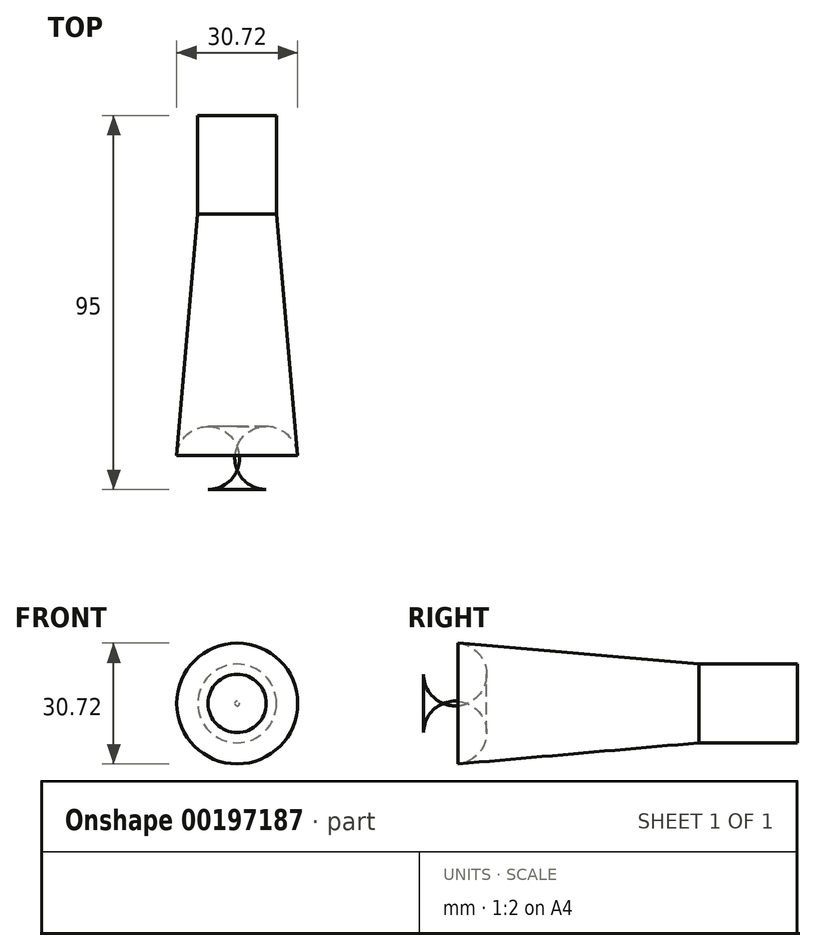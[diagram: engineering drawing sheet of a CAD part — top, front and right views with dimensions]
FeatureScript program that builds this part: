
annotation { "Feature Type Name" : "Feature", "Feature Type Description" : "" }
export const myFeature = defineFeature(function(context is Context, id is Id, definition is map)
    precondition{}
    {
        {
            var Q0;
            Q0=qCreatedBy(makeId("Front.planeOp"),FACE);
            var sketch = newSketch(context, id + "F0", { "sketchPlane" : qUnion([Q0])});
            skCircle(sketch, "E0", {"center": v(0, 0) * mm, "radius": 10 * mm});
            skSolve(sketch);
        }
        {
            var Q0;
            Q0 = qSketchRegion(id + "F0", true);
            extrude(context, id + "F1", {"entities" : qUnion([Q0]), "depth" : 70 * mm, "hasDraft" : true, "draftAngle" : 5 * degree});
        }
        {
            var Q0;
            Q0=makeQuery(id+"F1.opExtrude","CAP_EDGE",EDGE,{"disambiguationData":[OSD([sQuery(id+"F0.wireOp",EDGE,"E0")])],"isStart":false});
            fillet(context, id + "F2", {"entities" : qUnion([Q0]), "radius" : 8 * mm, "tangentPropagation" : true, "allowEdgeOverflow" : false});
        }
        {
            var Q0;
            Q0=makeQuery(id+"F1.opExtrude","CAP_FACE",FACE,{"disambiguationData":[OSD([sQuery(id+"F0.wireOp",EDGE,"E0")])],"isStart":true});
            var sketch = newSketch(context, id + "F3", { "sketchPlane" : qUnion([Q0])});
            skCircle(sketch, "E1", {"center": v(0, 0) * mm, "radius": 7.5 * mm});
            skSolve(sketch);
        }
        {
            var Q0;
            Q0=makeQuery(id+"F3.imprint","IMPRINT",FACE,{"disambiguationData":[TD([[makeQuery(id+"F3.imprint","IMPRINT",EDGE,{"derivedFrom":sQuery(id+"F3.wireOp",EDGE,"E1")}),-1.0]])]});
            var Q1;
            Q1=makeQuery(id+"F1.opExtrude","CAP_FACE",FACE,{"disambiguationData":[OSD([sQuery(id+"F0.wireOp",EDGE,"E0")])],"isStart":true});
            extrude(context, id + "F4", {"entities" : qUnion([Q0, Q1]), "operationType" : NewBodyOperationType.ADD, "depth" : 25 * mm});
        }
    });
